# Revit family: KDW030047
name_source: partatom
category: Plumbing Fixtures
revit_build: Autodesk Revit 2015 (Build: 20140606_1530(x64)
units: mm (PartAtom-declared; Revit-internal decimal feet)

## types (1)
- KDW030047
    Accessory = Yes
    Additional features of the object = https://www.kaldewei.co.uk
    BIMobject category = Basins
    Brand url = http://www.kaldewei.com
    Color = https://www.kaldewei.co.uk
    ColourOptions = https://www.kaldewei.co.uk
    Configurator link = https://www.kaldewei.co.uk
    Description details = KALDEWEI international Worldwide partner for iconic bathroom solutions made of KALDEWEI steel enamel  KALDEWEI steel enamel delivers unique advantages that inspire excellence in bathroom design. Projects across the world, from upmarket hotels to private homes, capture the sophisticated aesthetic that recommends KALDEWEI as the partner of choice. As a leading international manufacturer of high-quality shower surfaces, bathtubs and washbasins made of superior steel enamel, KALDEWEI today is present in more than 80 countries.
    Design country = Germany
    Durability = https://EN 14688
    Edition number = 1
    IFC Classification = Furnishing Element
    IfcExportAs = WASHHANDBASIN
    IfcExportType = IfcSanitaryTerminalType
    Link towards a photo of the product = https://www.kaldewei.co.uk
    Manufacturer country = Germany
    ManufacturerCountry = GERMANY
    ManufacturerName = KALDEWEI
    Material = steel enamel
    Material main = Steel
    Material secondary = Enamel
    NBS Reference Code = 35-65-70-94
    NBS Reference Description = Wash Basin Systems
    Name = MIENA bowl
    Nominal height = 400 cm
    Nominal width = 400 cm
    ObjectName = MIENA bowl 400x400
    ObjectNorm = EN 14688 EU DECLARATION OF PERFORMANCE (https://www.kaldewei.de
    Polantis code = KDW030047
    Product Guid = ac8ec725-e15d-4e3a-a61a-953c5a2300ba
    Product SKU = 3184
    Product certification = https://www.kaldewei.co.uk
    Product data url = http://bimobject.com
    Product family = MIENA
    Product group = Washbasin
    Product url = https://www.kaldewei.co.uk
    ProductInformation = Model No. 3184: The angular MIENA bowls are just as filigree but with a far more masculine look. Comparatively small radii, the only partially rounded contours and the square waste cover accentuate this effect – and extend the spectrum of the bowl family in the most elegant way.
    QR code = http://bimobject.com
    SerialNumber = 3184
    Shape = Bowl
    Size = 400x400
    Sound Insulation = DIN 4109:2016, VDI4100:2012
    Sustainability = https://EN 15804
    Technical data link = https://kaldewei.typo-live.web-factory.de
    Technical description = https://www.kaldewei.co.uk
    Type of accessories = https://www.kaldewei.co.uk
    Type of support framing = https://www.kaldewei.co.uk
    UNSPSC Code = 301815
    UNSPSCCode = 30181504
    UNSPSCNames = Sinks
    URL = https://www.kaldewei.com
    Uniclass 1.4 Code = L7212
    Uniclass 1.4 Description = Washbasins
    Uniclass 2.0 Code = SS-35-65-70-94
    Uniclass 2.0 Description = Wash Basin Systems
    Uniclass2 = Pr_40_20_96
    Version = 3
    WarrantyDurationParts = 30
    WarrantyDurationUnit = Year
    WarrantyStartDate = https://www.kaldewei.co.uk
    Website link = https://www.kaldewei.co.uk
    Weight = 8.9
    Weight Net (Kg) = 8.9

## geometry (parser evidence)
native form markers: Sweep x5
no freeform markers — native parametric forms only
